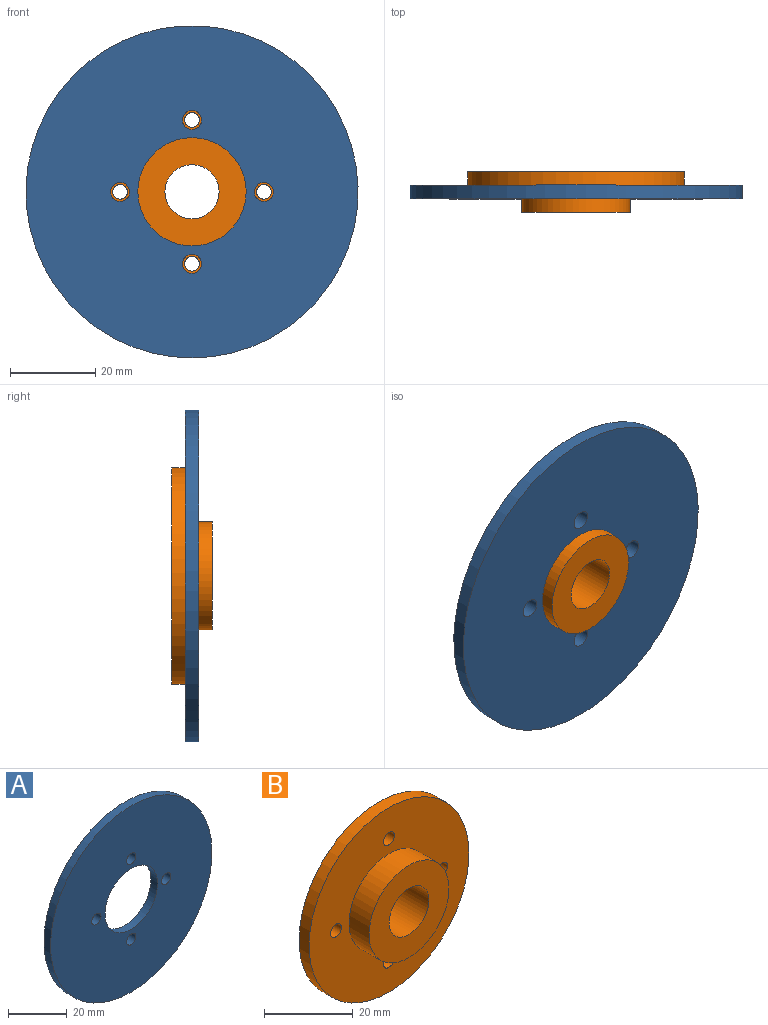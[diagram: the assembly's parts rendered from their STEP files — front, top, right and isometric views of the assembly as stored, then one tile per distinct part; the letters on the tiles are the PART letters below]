
ASSEMBLY  parts=2 mates=1
PART A: 8 faces, bbox 77.9x3.2x77.9 mm
  f0: plane 77.93x77.93mm, normal (0,1,0), area 4199.2mm2, adj f1,f3,f4,f5,f6,f7
  f1: cylinder r=38.96mm len=77.93mm, axis (0,-1,0), area 777.3mm2, adj f0,f2
  f2: plane 77.93x77.93mm, normal (0,-1,0), area 4199.2mm2, adj f1,f3,f4,f5,f6,f7
  f3: cylinder r=12.7mm len=25.4mm, axis (0,-1,0), area 253.4mm2, adj f0,f2
  f4: cylinder r=2.25mm len=4.5mm, axis (0,-1,0), area 44.8mm2, adj f0,f2
  f5: cylinder r=2.25mm len=4.5mm, axis (0,-1,0), area 44.8mm2, adj f0,f2
  f6: cylinder r=2.25mm len=4.5mm, axis (0,-1,0), area 44.8mm2, adj f0,f2
  f7: cylinder r=2.25mm len=4.5mm, axis (0,-1,0), area 44.8mm2, adj f0,f2
PART B: 10 faces, bbox 50.8x9.5x50.8 mm
  f0: cylinder r=6.35mm len=12.7mm, axis (0,-1,0), area 380mm2, adj f1,f5
  f1: plane 50.8x50.8mm, normal (0,1,0), area 1862.7mm2, adj f0,f2,f6,f7,f8,f9
  f2: cylinder r=25.4mm len=50.8mm, axis (0,-1,0), area 506.7mm2, adj f1,f3
  f3: plane 50.8x50.8mm, normal (0,-1,0), area 1482.6mm2, adj f2,f4,f6,f7,f8,f9
  f4: cylinder r=12.7mm len=25.4mm, axis (0,-1,0), area 506.7mm2, adj f3,f5
  f5: plane 25.4x25.4mm, normal (0,-1,0), area 380mm2, adj f0,f4
  f6: cylinder r=1.73mm len=3.45mm, axis (0,-1,0), area 34.5mm2, adj f1,f3
  f7: cylinder r=1.73mm len=3.45mm, axis (0,-1,0), area 34.5mm2, adj f1,f3
  f8: cylinder r=1.73mm len=3.45mm, axis (0,-1,0), area 34.5mm2, adj f1,f3
  f9: cylinder r=1.73mm len=3.45mm, axis (0,-1,0), area 34.5mm2, adj f1,f3
PLACE A t=(-0.04,0.07,0.14)mm
PLACE B t=(-0.04,0.07,0.14)mm
MATE fastened B.f6 <-> A.f5  axis (0,-1,0) through (-0.04,1.66,17.01)mm
